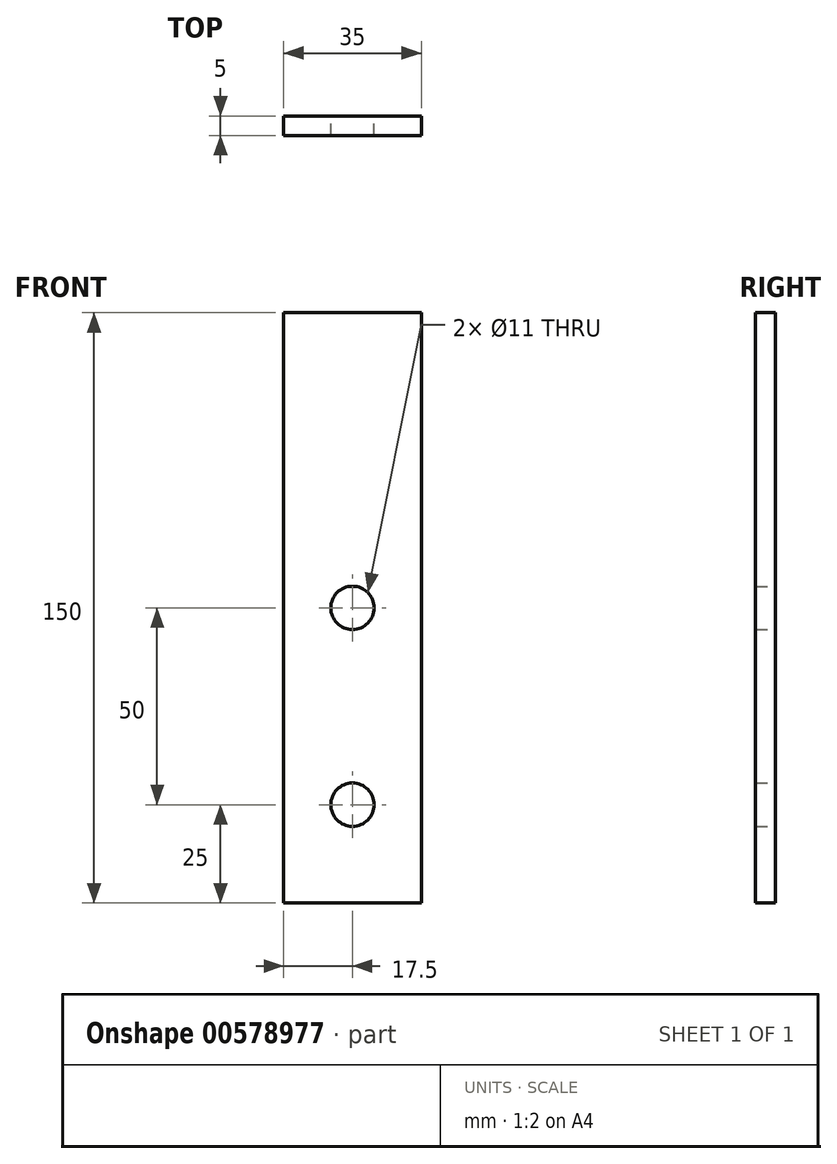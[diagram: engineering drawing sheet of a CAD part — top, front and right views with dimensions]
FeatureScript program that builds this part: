
annotation { "Feature Type Name" : "Feature", "Feature Type Description" : "" }
export const myFeature = defineFeature(function(context is Context, id is Id, definition is map)
    precondition{}
    {
        {
            var Q0;
            Q0=qCreatedBy(makeId("Front.planeOp"),FACE);
            var sketch = newSketch(context, id + "F0", { "sketchPlane" : qUnion([Q0])});
            skLineSegment(sketch, "E0.bottom", {"start": v(17.5, 75) * mm, "end": v(-17.5, 75) * mm});
            skLineSegment(sketch, "E0.top", {"start": v(17.5, -75) * mm, "end": v(-17.5, -75) * mm});
            skLineSegment(sketch, "E0.left", {"start": v(17.5, 75) * mm, "end": v(17.5, -75) * mm});
            skLineSegment(sketch, "E0.right", {"start": v(-17.5, 75) * mm, "end": v(-17.5, -75) * mm});
            skPoint(sketch, "E0.middle", {"position": v(0, 0) * mm});
            skCircle(sketch, "E1", {"center": v(0, 0) * mm, "radius": 5.5 * mm});
            skCircle(sketch, "E2", {"center": v(0, -50) * mm, "radius": 5.5 * mm});
            skPoint(sketch, "E2.centerSnap0", {"position": v(0, -75) * mm});
            skSolve(sketch);
        }
        {
            var Q0;
            Q0=makeQuery(id+"F0.imprint","IMPRINT",FACE,{"disambiguationData":[TD([[makeQuery(id+"F0.imprint","IMPRINT",EDGE,{"derivedFrom":sQuery(id+"F0.wireOp",EDGE,"E0.bottom")}),1.0]])]});
            extrude(context, id + "F1", {"entities" : qUnion([Q0]), "endBound" : BoundingType.SYMMETRIC, "depth" : 5 * mm, "offsetDistance" : 25 * mm});
        }
    });
